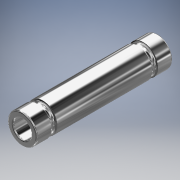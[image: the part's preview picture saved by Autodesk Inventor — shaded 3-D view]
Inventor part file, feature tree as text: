
AUTODESK INVENTOR PART (.ipt)
format: ipt  version: 2018 (Build 220112000, 112)  size: 165,888 bytes
history: native  units: mm
features: revolve x1, fillet x1, plane x1, sketch x1
ambient origin geometry x8: Origin, YZ Plane, XZ Plane, XY Plane, X Axis, Y Axis, Z Axis, Center Point
bodies: Solid1 (feature_tree)
feature tree (4):
  revolve  "Revolution1"  [1 undecoded]
  fillet  "Fillet1"  Radius=1.0mm
  plane  "Work Plane1"
  sketch  "Sketch1"  dims[d1=2.5mm d2=1.5mm d3=3.0mm d4=1.0mm d5=0.25mm d6=2.25mm d7=1.0mm d8=23.0mm d9=90.0deg d10=0.25mm]
note: 1 required parameter value undecoded (feature->parameter linkage not recoverable at this tier; creation-order binding heuristic only, values carry confidence <= 0.55)
